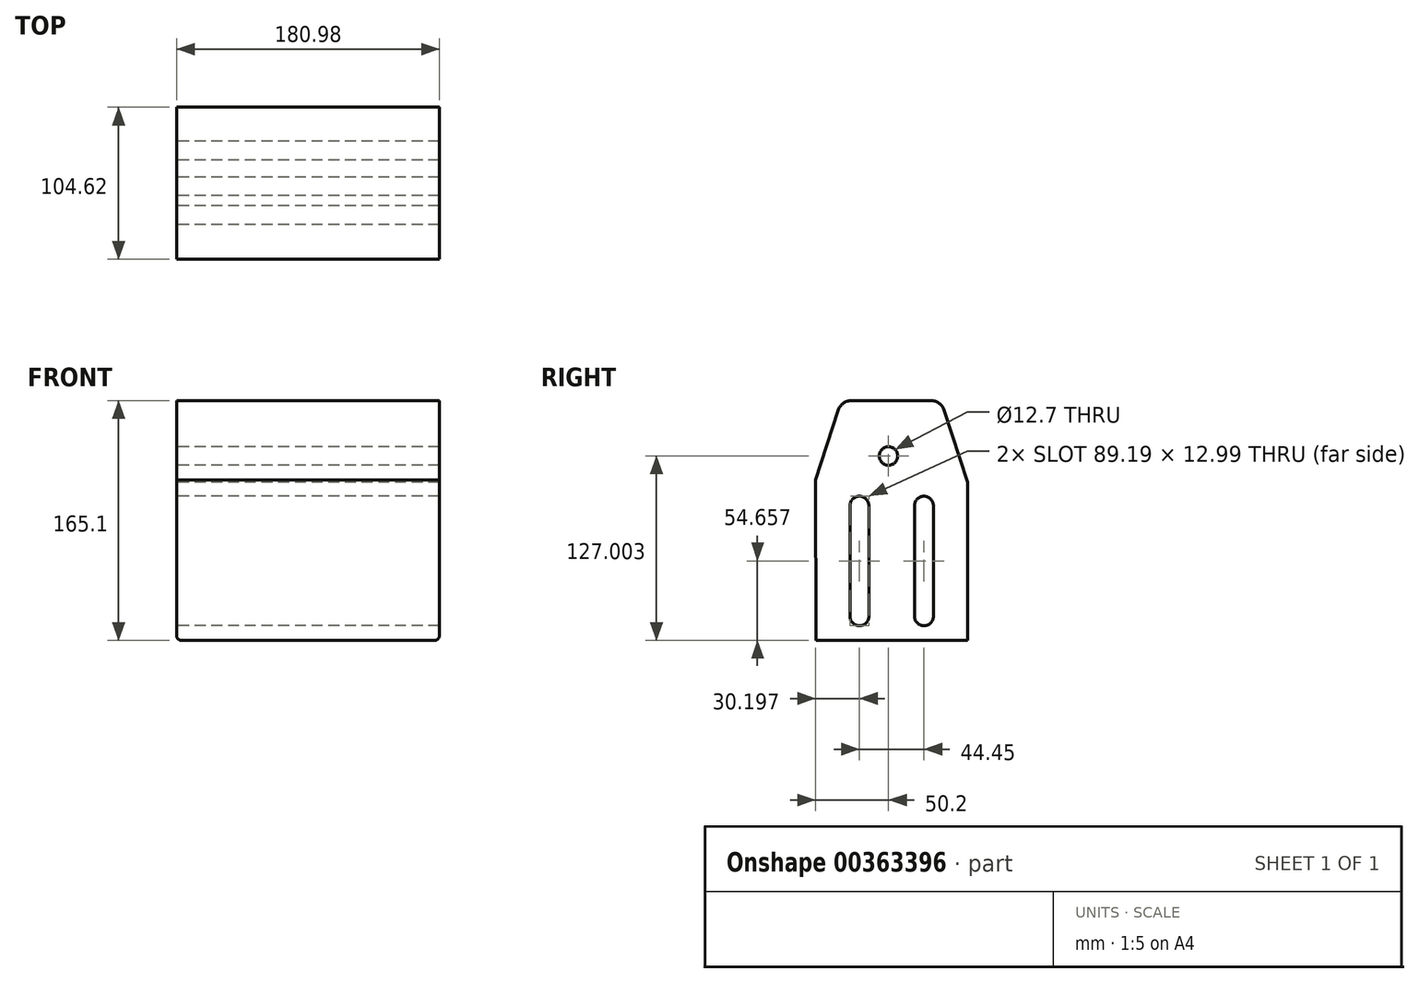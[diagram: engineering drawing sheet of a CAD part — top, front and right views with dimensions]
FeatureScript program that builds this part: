
annotation { "Feature Type Name" : "Feature", "Feature Type Description" : "" }
export const myFeature = defineFeature(function(context is Context, id is Id, definition is map)
    precondition{}
    {
        {
            var Q0;
            Q0=qCreatedBy(makeId("Right.planeOp"),FACE);
            var sketch = newSketch(context, id + "F0", { "sketchPlane" : qUnion([Q0])});
            skLineSegment(sketch, "E0.top", {"start": v(-49.98, -64.6) * mm, "end": v(54.42, -64.6) * mm});
            skLineSegment(sketch, "E0.right", {"start": v(54.42, 44.4) * mm, "end": v(54.42, -64.6) * mm});
            skCircle(sketch, "E1", {"center": v(0, 62.4) * mm, "radius": 6.35 * mm});
            skLineSegment(sketch, "E2.2", {"start": v(-50.2, 45.9) * mm, "end": v(-34.6, 93.91) * mm});
            skLineSegment(sketch, "E2.3", {"start": v(-25.54, 100.5) * mm, "end": v(29.27, 100.5) * mm});
            skLineSegment(sketch, "E2.4", {"start": v(38.33, 93.91) * mm, "end": v(54.42, 44.4) * mm});
            skPoint(sketch, "E3.orphan", {"position": v(54.42, 106.84) * mm});
            skPoint(sketch, "E4.orphan", {"position": v(50.2, 62.4) * mm});
            skPoint(sketch, "E5.orphan", {"position": v(0, 3.76) * mm});
            skPoint(sketch, "E6.orphan", {"position": v(-53.68, 35.2) * mm});
            skLineSegment(sketch, "E7.trimOffspring", {"start": v(-50.2, 45.9) * mm, "end": v(-49.98, -64.6) * mm});
            skPoint(sketch, "E8.orphan", {"position": v(-50.2, 62.4) * mm});
            skPoint(sketch, "E0.bottom.start.orphan", {"position": v(-47.18, 111) * mm});
            skPoint(sketch, "E9.visualSharp", {"position": v(-32.46, 100.5) * mm});
            skArc(sketch, "E9.filletArc", {"start": v(-25.54, 100.5) * mm, "mid": v(-31.14, 98.67) * mm, "end": v(-34.6, 93.91) * mm});
            skPoint(sketch, "E10.visualSharp", {"position": v(36.2, 100.5) * mm});
            skArc(sketch, "E10.filletArc", {"start": v(38.33, 93.91) * mm, "mid": v(34.87, 98.67) * mm, "end": v(29.27, 100.5) * mm});
            skArc(sketch, "E11", {"start": v(17.95, -48.05) * mm, "mid": v(24.45, -54.55) * mm, "end": v(30.94, -48.05) * mm});
            skArc(sketch, "E12.0.1.0", {"start": v(30.94, 28.15) * mm, "mid": v(24.45, 34.64) * mm, "end": v(17.95, 28.15) * mm});
            skArc(sketch, "E12.1.0.0", {"start": v(-26.5, -48.05) * mm, "mid": v(-20, -54.55) * mm, "end": v(-13.5, -48.05) * mm});
            skArc(sketch, "E12.1.1.0", {"start": v(-13.5, 28.15) * mm, "mid": v(-20, 34.64) * mm, "end": v(-26.5, 28.15) * mm});
            skLineSegment(sketch, "E12.direction1", {"start": v(17.95, -48.05) * mm, "end": v(-20, -48.05) * mm, "construction": true});
            skLineSegment(sketch, "E12.direction2", {"start": v(24.45, -48.05) * mm, "end": v(24.45, 28.15) * mm, "construction": true});
            skLineSegment(sketch, "E13", {"start": v(-26.5, 28.15) * mm, "end": v(-26.5, -48.05) * mm});
            skLineSegment(sketch, "E14", {"start": v(-13.5, 28.15) * mm, "end": v(-13.5, -48.05) * mm});
            skLineSegment(sketch, "E15", {"start": v(17.95, 28.15) * mm, "end": v(17.95, -48.05) * mm});
            skLineSegment(sketch, "E16", {"start": v(30.94, -48.05) * mm, "end": v(30.94, 28.15) * mm});
            skSolve(sketch);
        }
        {
            var Q0;
            Q0=makeQuery(id+"F0.imprint","IMPRINT",FACE,{"disambiguationData":[TD([[makeQuery(id+"F0.imprint","IMPRINT",EDGE,{"derivedFrom":sQuery(id+"F0.wireOp",EDGE,"E0.top")}),1.0]])]});
            extrude(context, id + "F1", {"entities" : qUnion([Q0]), "depth" : 180.97 * mm});
        }
        {
            var Q0;
            Q0=makeQuery(id+"F1.opExtrude","CAP_EDGE",EDGE,{"disambiguationData":[OSD([sQuery(id+"F0.wireOp",EDGE,"E0.top")])],"isStart":true});
            var Q1;
            Q1=makeQuery(id+"F1.opExtrude","CAP_EDGE",EDGE,{"disambiguationData":[OSD([sQuery(id+"F0.wireOp",EDGE,"E0.top")])],"isStart":false});
            fillet(context, id + "F2", {"entities" : qUnion([Q0, Q1]), "radius" : 3.17 * mm, "tangentPropagation" : true, "allowEdgeOverflow" : false});
        }
    });
